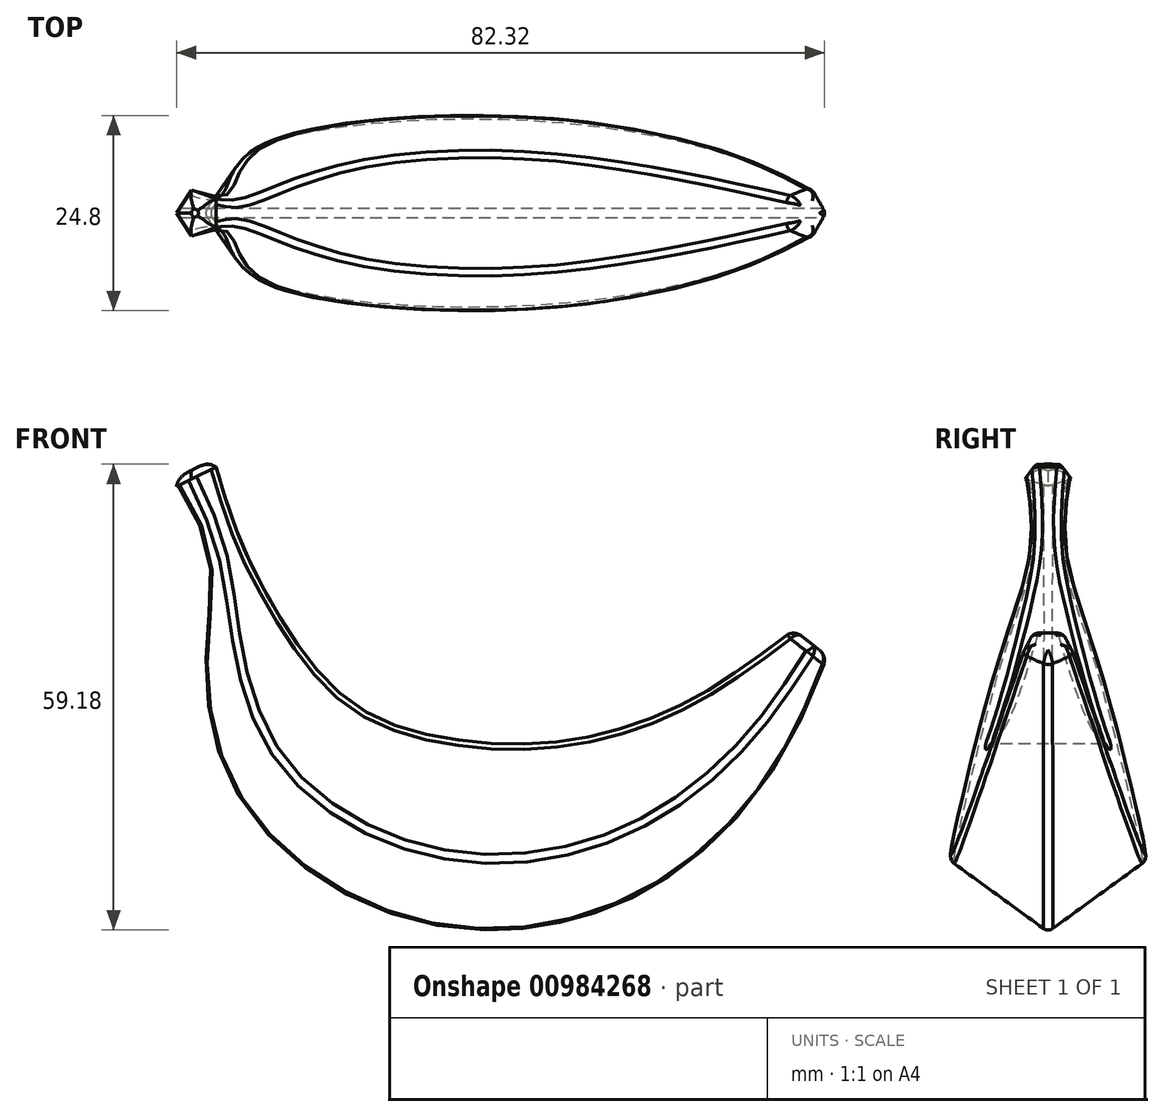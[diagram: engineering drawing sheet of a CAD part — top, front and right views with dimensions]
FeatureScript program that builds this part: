
annotation { "Feature Type Name" : "Feature", "Feature Type Description" : "" }
export const myFeature = defineFeature(function(context is Context, id is Id, definition is map)
    precondition{}
    {
        {
            var Q0;
            Q0=qCreatedBy(makeId("Front.planeOp"),FACE);
            var sketch = newSketch(context, id + "F0", { "sketchPlane" : qUnion([Q0])});
            skFitSpline(sketch, "E0", {"points": [v(-43.7, 21.14) * mm, v(-40.43, 12.76) * mm, v(-37, 0) * mm, v(-31.33, -12.38) * mm, v(-16.2, -22.06) * mm, v(4.59, -22.3) * mm, v(22.55, -12.61) * mm, v(33.9, 0) * mm], "startDerivative": vector(35.1, -72.04) * mm, "endDerivative": vector(56.2, 72.2) * mm});
            skSolve(sketch);
        }
        {
            var Q0;
            Q0=sQuery(id+"F0.wireOp",EDGE,"E0");
            var Q1;
            Q1=sQuery(id+"F0.wireOp",VERTEX,"E0.2.internal");
            cPlane(context, id + "F1", {"entities" : qUnion([Q0, Q1]), "cplaneType" : CPlaneType.CURVE_POINT, "offset" : 25.4 * mm, "width" : 152.4 * mm, "height" : 152.4 * mm});
        }
        {
            var Q0;
            Q0=sQuery(id+"F0.wireOp",EDGE,"E0");
            var Q1;
            Q1=sQuery(id+"F0.wireOp",VERTEX,"E0.start");
            cPlane(context, id + "F2", {"entities" : qUnion([Q0, Q1]), "cplaneType" : CPlaneType.CURVE_POINT, "offset" : 25.4 * mm, "width" : 152.4 * mm, "height" : 152.4 * mm});
        }
        {
            var Q0;
            Q0=sQuery(id+"F0.wireOp",EDGE,"E0");
            var Q1;
            Q1=sQuery(id+"F0.wireOp",VERTEX,"E0.1.internal");
            cPlane(context, id + "F3", {"entities" : qUnion([Q0, Q1]), "cplaneType" : CPlaneType.CURVE_POINT, "offset" : 25.4 * mm, "width" : 152.4 * mm, "height" : 152.4 * mm});
        }
        {
            var Q0;
            Q0=sQuery(id+"F0.wireOp",VERTEX,"E0.5.internal");
            var Q1;
            Q1=sQuery(id+"F0.wireOp",EDGE,"E0");
            cPlane(context, id + "F4", {"entities" : qUnion([Q0, Q1]), "cplaneType" : CPlaneType.CURVE_POINT, "offset" : 25.4 * mm, "width" : 152.4 * mm, "height" : 152.4 * mm});
        }
        {
            var Q0;
            Q0=sQuery(id+"F0.wireOp",VERTEX,"E0.end");
            var Q1;
            Q1=sQuery(id+"F0.wireOp",EDGE,"E0");
            cPlane(context, id + "F5", {"entities" : qUnion([Q0, Q1]), "cplaneType" : CPlaneType.CURVE_POINT, "offset" : 25.4 * mm, "width" : 152.4 * mm, "height" : 152.4 * mm});
        }
        {
            var Q0;
            Q0=qCreatedBy(id+"F2.planeOp",FACE);
            cPlane(context, id + "F6", {"entities" : qUnion([Q0]), "cplaneType" : CPlaneType.OFFSET, "offset" : 1 * mm, "oppositeDirection" : true, "width" : 152.4 * mm, "height" : 152.4 * mm});
        }
        {
            var Q0;
            Q0=qCreatedBy(id+"F5.planeOp",FACE);
            cPlane(context, id + "F7", {"entities" : qUnion([Q0]), "cplaneType" : CPlaneType.OFFSET, "offset" : 1 * mm, "width" : 152.4 * mm, "height" : 152.4 * mm});
        }
        {
            var Q0;
            Q0=qCreatedBy(id+"F2.planeOp",FACE);
            var sketch = newSketch(context, id + "F8", { "sketchPlane" : qUnion([Q0])});
            skPoint(sketch, "E1.0", {"position": v(-30.03, 0) * mm});
            skCircle(sketch, "E2.cCircle", {"center": v(-30.03, 0) * mm, "radius": 2.5 * mm, "construction": true});
            skLineSegment(sketch, "E2.0", {"start": v(-27.53, -1.82) * mm, "end": v(-30.99, -2.94) * mm});
            skLineSegment(sketch, "E2.1", {"start": v(-30.99, -2.94) * mm, "end": v(-33.12, 0) * mm});
            skLineSegment(sketch, "E2.2", {"start": v(-33.12, 0) * mm, "end": v(-30.99, 2.94) * mm});
            skLineSegment(sketch, "E2.3", {"start": v(-30.99, 2.94) * mm, "end": v(-27.53, 1.82) * mm});
            skLineSegment(sketch, "E2.4", {"start": v(-27.53, 1.82) * mm, "end": v(-27.53, -1.82) * mm});
            skPoint(sketch, "E2.0.midPoint", {"position": v(-29.26, -2.38) * mm});
            skSolve(sketch);
        }
        {
            var Q0;
            Q0=qCreatedBy(id+"F3.planeOp",FACE);
            var sketch = newSketch(context, id + "F9", { "sketchPlane" : qUnion([Q0])});
            skPoint(sketch, "E3.0", {"position": v(-34.93, 0) * mm});
            skCircle(sketch, "E4.cCircle", {"center": v(-34.93, 0) * mm, "radius": 2 * mm, "construction": true});
            skLineSegment(sketch, "E4.0", {"start": v(-32.93, -1.45) * mm, "end": v(-35.7, -2.35) * mm});
            skLineSegment(sketch, "E4.1", {"start": v(-35.7, -2.35) * mm, "end": v(-37.4, 0) * mm});
            skLineSegment(sketch, "E4.2", {"start": v(-37.4, 0) * mm, "end": v(-35.7, 2.35) * mm});
            skLineSegment(sketch, "E4.3", {"start": v(-35.7, 2.35) * mm, "end": v(-32.93, 1.45) * mm});
            skLineSegment(sketch, "E4.4", {"start": v(-32.93, 1.45) * mm, "end": v(-32.93, -1.45) * mm});
            skPoint(sketch, "E4.0.midPoint", {"position": v(-34.32, -1.9) * mm});
            skSolve(sketch);
        }
        {
            var Q0;
            Q0=qCreatedBy(id+"F1.planeOp",FACE);
            var sketch = newSketch(context, id + "F10", { "sketchPlane" : qUnion([Q0])});
            skPoint(sketch, "E5.0", {"position": v(-35.64, 0) * mm});
            skCircle(sketch, "E6.cCircle", {"center": v(-35.64, 0) * mm, "radius": 5 * mm, "construction": true});
            skLineSegment(sketch, "E6.0", {"start": v(-30.64, -3.63) * mm, "end": v(-37.55, -5.88) * mm});
            skLineSegment(sketch, "E6.1", {"start": v(-37.55, -5.88) * mm, "end": v(-41.82, 0) * mm});
            skLineSegment(sketch, "E6.2", {"start": v(-41.82, 0) * mm, "end": v(-37.55, 5.88) * mm});
            skLineSegment(sketch, "E6.3", {"start": v(-37.55, 5.88) * mm, "end": v(-30.64, 3.63) * mm});
            skLineSegment(sketch, "E6.4", {"start": v(-30.64, 3.63) * mm, "end": v(-30.64, -3.63) * mm});
            skPoint(sketch, "E6.0.midPoint", {"position": v(-34.1, -4.76) * mm});
            skSolve(sketch);
        }
        {
            var Q0;
            Q0=qCreatedBy(id+"F5.planeOp",FACE);
            var sketch = newSketch(context, id + "F11", { "sketchPlane" : qUnion([Q0])});
            skPoint(sketch, "E7.0", {"position": v(26.74, 0) * mm});
            skCircle(sketch, "E8.cCircle", {"center": v(26.74, 0) * mm, "radius": 2.5 * mm, "construction": true});
            skLineSegment(sketch, "E8.0", {"start": v(29.83, 0) * mm, "end": v(27.7, -2.94) * mm});
            skLineSegment(sketch, "E8.1", {"start": v(27.7, -2.94) * mm, "end": v(24.24, -1.82) * mm});
            skLineSegment(sketch, "E8.2", {"start": v(24.24, -1.82) * mm, "end": v(24.24, 1.82) * mm});
            skLineSegment(sketch, "E8.3", {"start": v(24.24, 1.82) * mm, "end": v(27.7, 2.94) * mm});
            skLineSegment(sketch, "E8.4", {"start": v(27.7, 2.94) * mm, "end": v(29.83, 0) * mm});
            skPoint(sketch, "E8.0.midPoint", {"position": v(28.77, -1.47) * mm});
            skSolve(sketch);
        }
        {
            var Q0;
            Q0=qCreatedBy(id+"F4.planeOp",FACE);
            var sketch = newSketch(context, id + "F12", { "sketchPlane" : qUnion([Q0])});
            skPoint(sketch, "E9.0", {"position": v(0, -22.74) * mm});
            skCircle(sketch, "E10.cCircle", {"center": v(0, -22.74) * mm, "radius": 10 * mm, "construction": true});
            skLineSegment(sketch, "E10.0", {"start": v(7.27, -12.74) * mm, "end": v(11.76, -26.56) * mm});
            skLineSegment(sketch, "E10.1", {"start": v(11.76, -26.56) * mm, "end": v(0, -35.1) * mm});
            skLineSegment(sketch, "E10.2", {"start": v(0, -35.1) * mm, "end": v(-11.76, -26.56) * mm});
            skLineSegment(sketch, "E10.3", {"start": v(-11.76, -26.56) * mm, "end": v(-7.27, -12.74) * mm});
            skLineSegment(sketch, "E10.4", {"start": v(-7.27, -12.74) * mm, "end": v(7.27, -12.74) * mm});
            skPoint(sketch, "E10.0.midPoint", {"position": v(9.51, -19.65) * mm});
            skSolve(sketch);
        }
        {
            var Q0;
            Q0=qCreatedBy(id+"F6.planeOp",FACE);
            var sketch = newSketch(context, id + "F13", { "sketchPlane" : qUnion([Q0])});
            skPoint(sketch, "E11.0", {"position": v(-30.03, 0) * mm});
            skCircle(sketch, "E12", {"center": v(-30.03, 0) * mm, "radius": 0.5 * mm});
            skSolve(sketch);
        }
        {
            var Q0;
            Q0=sQuery(id+"F0.wireOp",EDGE,"E0");
            var Q1;
            Q1 = qSketchRegion(id + "F8", true);
            var Q2;
            Q2 = qSketchRegion(id + "F9", true);
            var Q3;
            Q3 = qSketchRegion(id + "F10", true);
            var Q4;
            Q4 = qSketchRegion(id + "F12", true);
            var Q5;
            Q5 = qSketchRegion(id + "F11", true);
            var Q6;
            Q6=sQuery(id+"F0.wireOp",EDGE,"E0");
            loft(context, id + "F14", {"addSections" : true, "spine" : qUnion([Q0]), "sectionCount" : 5, "sheetProfilesArray" : [{ "sheetProfileEntities" : qUnion([Q1]) }, { "sheetProfileEntities" : qUnion([Q2]) }, { "sheetProfileEntities" : qUnion([Q3]) }, { "sheetProfileEntities" : qUnion([Q4]) }, { "sheetProfileEntities" : qUnion([Q5]) }], "guidesArray" : [{ "guideEntities" : qUnion([Q6]), "guideDerivativeType" : LoftGuideDerivativeType.DEFAULT, "guideDerivativeMagnitude" : 1 }]});
        }
        {
            var Q0;
            Q0=makeQuery(id+"F14.opLoft","MID_CAP_EDGE",EDGE,{"disambiguationData":[OSD([sQuery(id+"F11.wireOp",EDGE,"E8.0"),sQuery(id+"F11.wireOp",EDGE,"E8.1"),sQuery(id+"F11.wireOp",EDGE,"E8.2")])],"capPos":4.0});
            var Q1;
            Q1=makeQuery(id+"F14.opLoft","MID_CAP_EDGE",EDGE,{"disambiguationData":[OSD([sQuery(id+"F11.wireOp",EDGE,"E8.1"),sQuery(id+"F11.wireOp",EDGE,"E8.2"),sQuery(id+"F11.wireOp",EDGE,"E8.3")])],"capPos":4.0});
            var Q2;
            Q2=makeQuery(id+"F14.opLoft","MID_CAP_EDGE",EDGE,{"disambiguationData":[OSD([sQuery(id+"F11.wireOp",EDGE,"E8.0"),sQuery(id+"F11.wireOp",EDGE,"E8.3"),sQuery(id+"F11.wireOp",EDGE,"E8.4")])],"capPos":4.0});
            var Q3;
            Q3=makeQuery(id+"F14.opLoft","MID_CAP_EDGE",EDGE,{"disambiguationData":[OSD([sQuery(id+"F11.wireOp",EDGE,"E8.0"),sQuery(id+"F11.wireOp",EDGE,"E8.1"),sQuery(id+"F11.wireOp",EDGE,"E8.4")])],"capPos":4.0});
            var Q4;
            Q4=makeQuery(id+"F14.opLoft","MID_CAP_EDGE",EDGE,{"disambiguationData":[OSD([sQuery(id+"F11.wireOp",EDGE,"E8.2"),sQuery(id+"F11.wireOp",EDGE,"E8.3"),sQuery(id+"F11.wireOp",EDGE,"E8.4")])],"capPos":4.0});
            fillet(context, id + "F15", {"entities" : qUnion([Q0, Q1, Q2, Q3, Q4]), "radius" : 1.5 * mm, "tangentPropagation" : true, "allowEdgeOverflow" : false});
        }
        {
            var Q0;
            Q0 = qSketchRegion(id + "F13", true);
            var Q1;
            Q1 = qSketchRegion(id + "F8", true);
            loft(context, id + "F16", {"startCondition" : LoftEndDerivativeType.TANGENT_TO_PROFILE, "startMagnitude" : 2, "sheetProfilesArray" : [{ "sheetProfileEntities" : qUnion([Q0]) }, { "sheetProfileEntities" : qUnion([Q1]) }]});
        }
        {
            var Q0;
            Q0=makeQuery(id+"F14.opLoft","SWEPT_EDGE",EDGE,{"disambiguationData":[OSD([sQuery(id+"F8.wireOp",EDGE,"E2.3"),sQuery(id+"F8.wireOp",EDGE,"E2.4"),sQuery(id+"F9.wireOp",EDGE,"E4.3"),sQuery(id+"F9.wireOp",EDGE,"E4.4"),sQuery(id+"F10.wireOp",EDGE,"E6.3"),sQuery(id+"F10.wireOp",EDGE,"E6.4"),sQuery(id+"F11.wireOp",EDGE,"E8.1"),sQuery(id+"F11.wireOp",EDGE,"E8.2"),sQuery(id+"F12.wireOp",EDGE,"E10.3"),sQuery(id+"F12.wireOp",EDGE,"E10.4")])]});
            var Q1;
            Q1=makeQuery(id+"F14.opLoft","SWEPT_EDGE",EDGE,{"disambiguationData":[OSD([sQuery(id+"F8.wireOp",EDGE,"E2.0"),sQuery(id+"F8.wireOp",EDGE,"E2.4"),sQuery(id+"F9.wireOp",EDGE,"E4.0"),sQuery(id+"F9.wireOp",EDGE,"E4.4"),sQuery(id+"F10.wireOp",EDGE,"E6.0"),sQuery(id+"F10.wireOp",EDGE,"E6.4"),sQuery(id+"F11.wireOp",EDGE,"E8.2"),sQuery(id+"F11.wireOp",EDGE,"E8.3"),sQuery(id+"F12.wireOp",EDGE,"E10.0"),sQuery(id+"F12.wireOp",EDGE,"E10.4")])]});
            var Q2;
            Q2=makeQuery(id+"F14.opLoft","SWEPT_EDGE",EDGE,{"disambiguationData":[OSD([sQuery(id+"F8.wireOp",EDGE,"E2.0"),sQuery(id+"F8.wireOp",EDGE,"E2.1"),sQuery(id+"F9.wireOp",EDGE,"E4.0"),sQuery(id+"F9.wireOp",EDGE,"E4.1"),sQuery(id+"F10.wireOp",EDGE,"E6.0"),sQuery(id+"F10.wireOp",EDGE,"E6.1"),sQuery(id+"F11.wireOp",EDGE,"E8.3"),sQuery(id+"F11.wireOp",EDGE,"E8.4"),sQuery(id+"F12.wireOp",EDGE,"E10.0"),sQuery(id+"F12.wireOp",EDGE,"E10.1")])]});
            var Q3;
            Q3=makeQuery(id+"F14.opLoft","SWEPT_EDGE",EDGE,{"disambiguationData":[OSD([sQuery(id+"F8.wireOp",EDGE,"E2.2"),sQuery(id+"F8.wireOp",EDGE,"E2.3"),sQuery(id+"F9.wireOp",EDGE,"E4.2"),sQuery(id+"F9.wireOp",EDGE,"E4.3"),sQuery(id+"F10.wireOp",EDGE,"E6.2"),sQuery(id+"F10.wireOp",EDGE,"E6.3"),sQuery(id+"F11.wireOp",EDGE,"E8.0"),sQuery(id+"F11.wireOp",EDGE,"E8.1"),sQuery(id+"F12.wireOp",EDGE,"E10.2"),sQuery(id+"F12.wireOp",EDGE,"E10.3")])]});
            var Q4;
            Q4=makeQuery(id+"F14.opLoft","SWEPT_EDGE",EDGE,{"disambiguationData":[OSD([sQuery(id+"F8.wireOp",EDGE,"E2.1"),sQuery(id+"F8.wireOp",EDGE,"E2.2"),sQuery(id+"F9.wireOp",EDGE,"E4.1"),sQuery(id+"F9.wireOp",EDGE,"E4.2"),sQuery(id+"F10.wireOp",EDGE,"E6.1"),sQuery(id+"F10.wireOp",EDGE,"E6.2"),sQuery(id+"F11.wireOp",EDGE,"E8.0"),sQuery(id+"F11.wireOp",EDGE,"E8.4"),sQuery(id+"F12.wireOp",EDGE,"E10.1"),sQuery(id+"F12.wireOp",EDGE,"E10.2")])]});
            fillet(context, id + "F17", {"entities" : qUnion([Q0, Q1, Q2, Q3, Q4]), "radius" : 1 * mm, "tangentPropagation" : true, "allowEdgeOverflow" : false});
        }
    });
